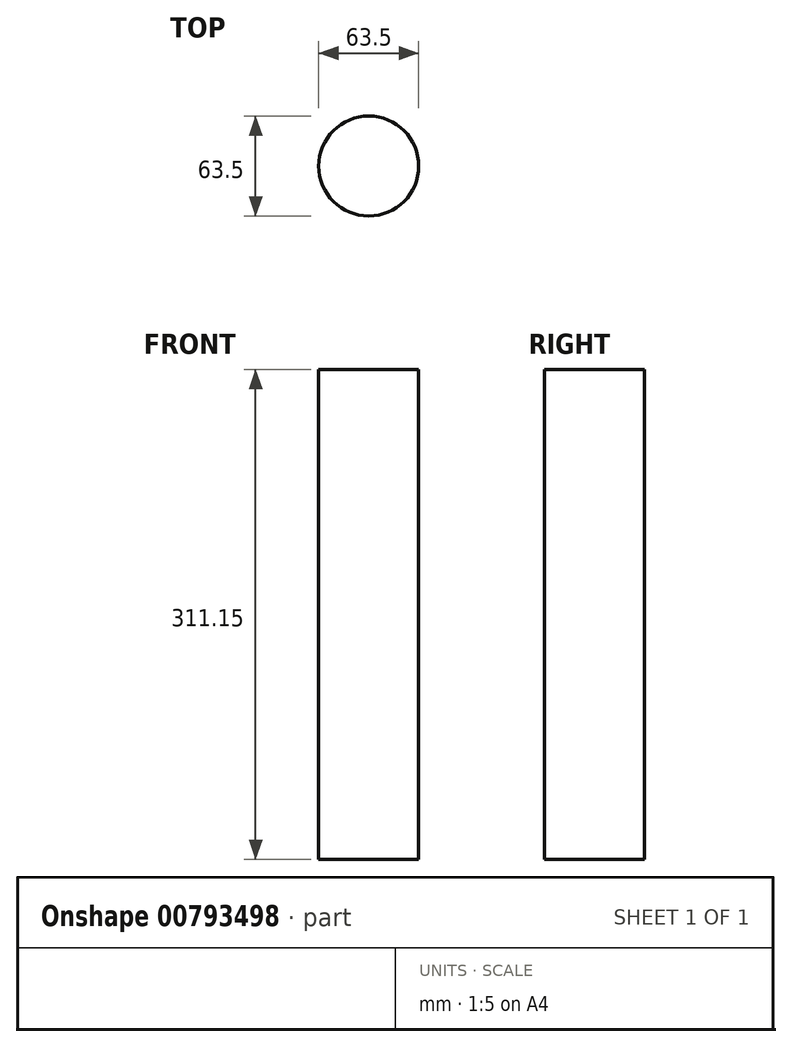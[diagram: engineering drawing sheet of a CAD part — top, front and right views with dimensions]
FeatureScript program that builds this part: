
annotation { "Feature Type Name" : "Feature", "Feature Type Description" : "" }
export const myFeature = defineFeature(function(context is Context, id is Id, definition is map)
    precondition{}
    {
        {
            var Q0;
            Q0=qCreatedBy(makeId("Top.planeOp"),FACE);
            var sketch = newSketch(context, id + "F0", { "sketchPlane" : qUnion([Q0])});
            skCircle(sketch, "E0", {"center": v(0, 0) * mm, "radius": 31.75 * mm});
            skSolve(sketch);
        }
        {
            var Q0;
            Q0 = qSketchRegion(id + "F0", true);
            extrude(context, id + "F1", {"entities" : qUnion([Q0]), "depth" : 311.15 * mm, "offsetDistance" : 25.4 * mm});
        }
    });
